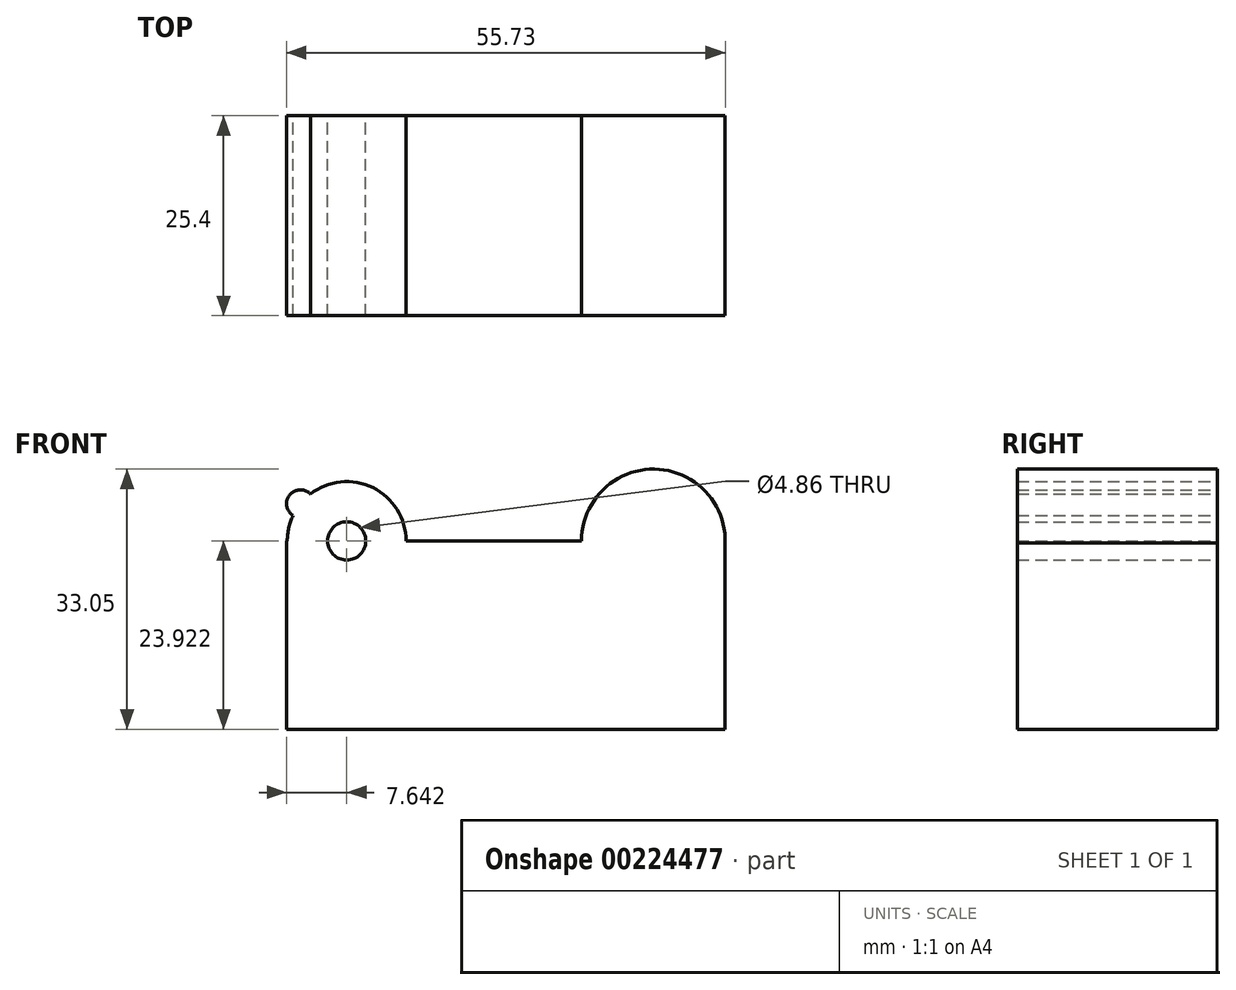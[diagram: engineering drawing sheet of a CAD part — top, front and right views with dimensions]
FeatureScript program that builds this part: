
annotation { "Feature Type Name" : "Feature", "Feature Type Description" : "" }
export const myFeature = defineFeature(function(context is Context, id is Id, definition is map)
    precondition{}
    {
        {
            var Q0;
            Q0=qCreatedBy(makeId("Front.planeOp"),FACE);
            var sketch = newSketch(context, id + "F0", { "sketchPlane" : qUnion([Q0])});
            skLineSegment(sketch, "E0", {"start": v(-55.97, 43.77) * mm, "end": v(25.4, 43.77) * mm});
            skLineSegment(sketch, "E1.bottom", {"start": v(-27.86, 12.45) * mm, "end": v(27.86, 12.45) * mm});
            skLineSegment(sketch, "E1.top", {"start": v(-27.86, -11.47) * mm, "end": v(27.86, -11.47) * mm});
            skLineSegment(sketch, "E1.left", {"start": v(-27.86, 12.45) * mm, "end": v(-27.86, -11.47) * mm});
            skLineSegment(sketch, "E1.right", {"start": v(27.86, 12.45) * mm, "end": v(27.86, -11.47) * mm});
            skCircle(sketch, "E2", {"center": v(-20.22, 12.45) * mm, "radius": 7.54 * mm});
            skCircle(sketch, "E3", {"center": v(18.74, 12.45) * mm, "radius": 9.13 * mm});
            skCircle(sketch, "E4", {"center": v(-20.22, 12.45) * mm, "radius": 2.43 * mm});
            skCircle(sketch, "E5", {"center": v(-26.1, 17.18) * mm, "radius": 1.77 * mm});
            skSolve(sketch);
        }
        {
            var Q0;
            Q0=makeQuery(id+"F0.imprint","IMPRINT",FACE,{"disambiguationData":[TD([[makeQuery(id+"F0.imprint","IMPRINT",EDGE,{"derivedFrom":sQuery(id+"F0.wireOp",EDGE,"E1.bottom")}),-1.0]])]});
            extrude(context, id + "F1", {"entities" : qUnion([Q0]), "depth" : 25.4 * mm});
        }
        {
            var Q0;
            Q0=sQuery(id+"F0.wireOp",EDGE,"E0");
            extrude(context, id + "F2", {"bodyType" : ToolBodyType.SURFACE, "surfaceEntities" : qUnion([Q0]), "depth" : 25.4 * mm});
        }
        {
            var Q0;
            Q0 = qSketchRegion(id + "F0", true);
            extrude(context, id + "F3", {"entities" : qUnion([Q0]), "operationType" : NewBodyOperationType.ADD, "depth" : 25.4 * mm});
        }
    });
